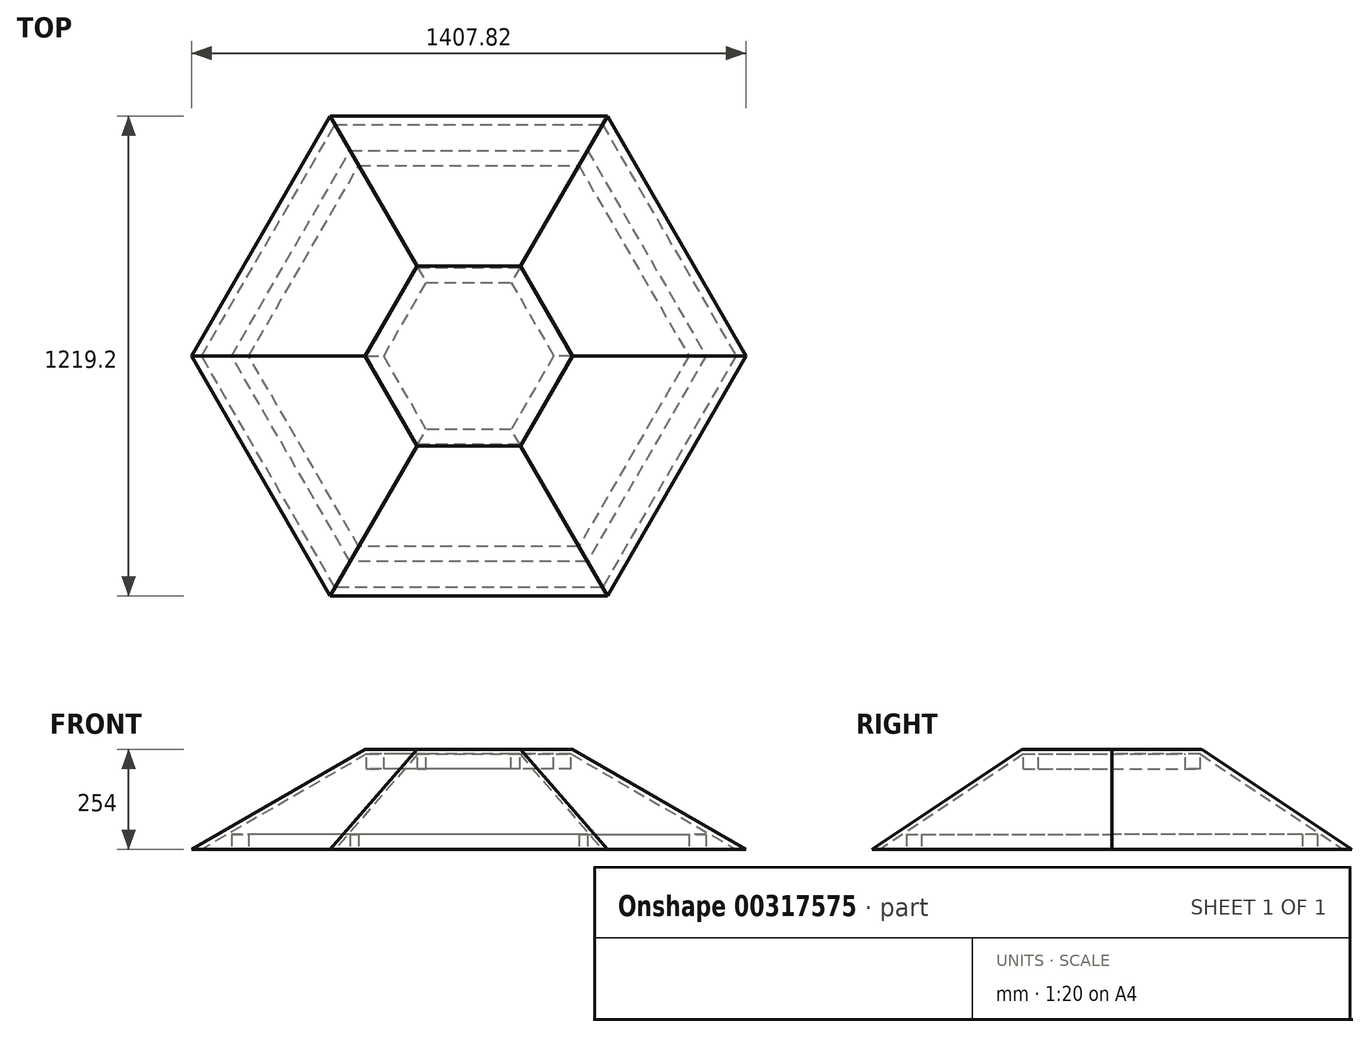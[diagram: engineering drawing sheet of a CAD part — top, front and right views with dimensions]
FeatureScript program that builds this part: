
annotation { "Feature Type Name" : "Feature", "Feature Type Description" : "" }
export const myFeature = defineFeature(function(context is Context, id is Id, definition is map)
    precondition{}
    {
        {
            var Q0;
            Q0=qCreatedBy(makeId("Top.planeOp"),FACE);
            var sketch = newSketch(context, id + "F0", { "sketchPlane" : qUnion([Q0])});
            skCircle(sketch, "E0.cCircle", {"center": v(0, 0) * mm, "radius": 609.6 * mm, "construction": true});
            skLineSegment(sketch, "E0.0", {"start": v(703.9, 0) * mm, "end": v(351.95, -609.6) * mm});
            skLineSegment(sketch, "E0.1", {"start": v(351.95, -609.6) * mm, "end": v(-351.95, -609.6) * mm});
            skLineSegment(sketch, "E0.2", {"start": v(-351.95, -609.6) * mm, "end": v(-703.9, 0) * mm});
            skLineSegment(sketch, "E0.3", {"start": v(-703.9, 0) * mm, "end": v(-351.95, 609.6) * mm});
            skLineSegment(sketch, "E0.4", {"start": v(-351.95, 609.6) * mm, "end": v(351.95, 609.6) * mm});
            skLineSegment(sketch, "E0.5", {"start": v(351.95, 609.6) * mm, "end": v(703.9, 0) * mm});
            skPoint(sketch, "E0.0.midPoint", {"position": v(527.93, -304.8) * mm});
            skSolve(sketch);
        }
        {
            var Q0;
            Q0=qCreatedBy(makeId("Front.planeOp"),FACE);
            var sketch = newSketch(context, id + "F1", { "sketchPlane" : qUnion([Q0])});
            skPoint(sketch, "E1.0", {"position": v(-703.9, 0) * mm});
            skPoint(sketch, "E2.0", {"position": v(703.9, 0) * mm});
            skLineSegment(sketch, "E3", {"start": v(703.9, 0) * mm, "end": v(263.96, 254) * mm});
            skLineSegment(sketch, "E4", {"start": v(263.96, 254) * mm, "end": v(-263.96, 254) * mm});
            skLineSegment(sketch, "E5", {"start": v(-263.96, 254) * mm, "end": v(-703.9, 0) * mm});
            skLineSegment(sketch, "E6", {"start": v(0, 0) * mm, "end": v(0, 391.16) * mm, "construction": true});
            skPoint(sketch, "E6.endSnap0", {"position": v(0, 254) * mm});
            skSolve(sketch);
        }
        {
            var Q0;
            Q0=makeQuery(id+"F0.imprint","IMPRINT",FACE,{"disambiguationData":[TD([[makeQuery(id+"F0.imprint","IMPRINT",EDGE,{"derivedFrom":sQuery(id+"F0.wireOp",EDGE,"E0.0")}),-1.0]])]});
            cPlane(context, id + "F2", {"entities" : qUnion([Q0]), "cplaneType" : CPlaneType.OFFSET, "offset" : 254 * mm, "width" : 152.4 * mm, "height" : 152.4 * mm});
        }
        {
            var Q0;
            Q0=qCreatedBy(id+"F2.planeOp",FACE);
            var sketch = newSketch(context, id + "F3", { "sketchPlane" : qUnion([Q0])});
            skCircle(sketch, "E7.cCircle", {"center": v(0, 0) * mm, "radius": 228.6 * mm, "construction": true});
            skLineSegment(sketch, "E7.0", {"start": v(263.96, 0) * mm, "end": v(131.98, -228.6) * mm});
            skLineSegment(sketch, "E7.1", {"start": v(131.98, -228.6) * mm, "end": v(-131.98, -228.6) * mm});
            skLineSegment(sketch, "E7.2", {"start": v(-131.98, -228.6) * mm, "end": v(-263.96, 0) * mm});
            skLineSegment(sketch, "E7.3", {"start": v(-263.96, 0) * mm, "end": v(-131.98, 228.6) * mm});
            skLineSegment(sketch, "E7.4", {"start": v(-131.98, 228.6) * mm, "end": v(131.98, 228.6) * mm});
            skLineSegment(sketch, "E7.5", {"start": v(131.98, 228.6) * mm, "end": v(263.96, 0) * mm});
            skPoint(sketch, "E7.0.midPoint", {"position": v(228.6, 0) * mm});
            skSolve(sketch);
        }
        {
            var Q0;
            Q0=makeQuery(id+"F3.imprint","IMPRINT",FACE,{"disambiguationData":[TD([[makeQuery(id+"F3.imprint","IMPRINT",EDGE,{"derivedFrom":sQuery(id+"F3.wireOp",EDGE,"E7.0")}),-1.0]])]});
            var Q1;
            Q1=makeQuery(id+"F0.imprint","IMPRINT",FACE,{"disambiguationData":[TD([[makeQuery(id+"F0.imprint","IMPRINT",EDGE,{"derivedFrom":sQuery(id+"F0.wireOp",EDGE,"E0.0")}),-1.0]])]});
            var Q2;
            Q2=sQuery(id+"F0.wireOp",VERTEX,"E0.2.start");
            var Q3;
            Q3=sQuery(id+"F3.wireOp",VERTEX,"E7.2.start");
            loft(context, id + "F4", {"sheetProfilesArray" : [{ "sheetProfileEntities" : qUnion([Q0]) }, { "sheetProfileEntities" : qUnion([Q1]) }], "connections" : [{ "connectionEntities" : qUnion([Q2, Q3]), "connectionEdgeQueries" : qUnion([]), "connectionEdgeParameters" : [] }]});
        }
        {
            var Q0;
            Q0=makeQuery(id+"F4.opLoft","CAP_FACE",FACE,{"disambiguationData":[OSD([makeQuery(id+"F0.imprint","IMPRINT",FACE,{"disambiguationData":[TD([[makeQuery(id+"F0.imprint","IMPRINT",EDGE,{"derivedFrom":sQuery(id+"F0.wireOp",EDGE,"E0.0")}),-1.0]])]})])],"isStart":true});
            shell(context, id + "F5", {"entities" : qUnion([Q0]), "thickness" : 11.9 * mm});
        }
        {
            var Q0;
            Q0=makeQuery(id+"F5.opShell","OFFSET_FACE",FACE,{"disambiguationData":[OSD([makeQuery(id+"F3.imprint","IMPRINT",FACE,{"disambiguationData":[TD([[makeQuery(id+"F3.imprint","IMPRINT",EDGE,{"derivedFrom":sQuery(id+"F3.wireOp",EDGE,"E7.0")}),-1.0]])]})])]});
            var sketch = newSketch(context, id + "F6", { "sketchPlane" : qUnion([Q0])});
            skLineSegment(sketch, "E8.0", {"start": v(-129.9, -225) * mm, "end": v(129.9, -225) * mm});
            skLineSegment(sketch, "E9.0", {"start": v(-107.9, -186.9) * mm, "end": v(107.9, -186.9) * mm});
            skLineSegment(sketch, "E10", {"start": v(-129.9, -225) * mm, "end": v(-107.9, -186.9) * mm});
            skLineSegment(sketch, "E11", {"start": v(129.9, -225) * mm, "end": v(107.9, -186.9) * mm});
            skSolve(sketch);
        }
        {
            var Q0;
            Q0=makeQuery(id+"F6.imprint","IMPRINT",FACE,{"disambiguationData":[TD([[makeQuery(id+"F6.imprint","IMPRINT",EDGE,{"derivedFrom":sQuery(id+"F6.wireOp",EDGE,"E8.0")}),1.0]])]});
            extrude(context, id + "F7", {"entities" : qUnion([Q0]), "depth" : 38.1 * mm});
        }
        {
            var Q0;
            Q0=makeQuery(id+"F0.imprint","IMPRINT",FACE,{"disambiguationData":[TD([[makeQuery(id+"F0.imprint","IMPRINT",EDGE,{"derivedFrom":sQuery(id+"F0.wireOp",EDGE,"E0.0")}),-1.0]])]});
            var sketch = newSketch(context, id + "F8", { "sketchPlane" : qUnion([Q0])});
            skLineSegment(sketch, "E12.0", {"start": v(-339.56, 588.14) * mm, "end": v(339.56, 588.14) * mm});
            skLineSegment(sketch, "E13.0", {"start": v(-301.48, 522.17) * mm, "end": v(301.48, 522.17) * mm});
            skLineSegment(sketch, "E14.0", {"start": v(-279.48, 484.07) * mm, "end": v(279.48, 484.07) * mm});
            skLineSegment(sketch, "E15", {"start": v(-301.48, 522.17) * mm, "end": v(-279.48, 484.07) * mm});
            skLineSegment(sketch, "E16", {"start": v(301.48, 522.17) * mm, "end": v(279.48, 484.07) * mm});
            skSolve(sketch);
        }
        {
            var Q0;
            Q0=makeQuery(id+"F8.imprint","IMPRINT",FACE,{"disambiguationData":[TD([[makeQuery(id+"F8.imprint","IMPRINT",EDGE,{"derivedFrom":sQuery(id+"F8.wireOp",EDGE,"E13.0")}),-1.0]])]});
            extrude(context, id + "F9", {"entities" : qUnion([Q0]), "operationType" : NewBodyOperationType.ADD, "depth" : 38.1 * mm});
        }
        {
            var Q0;
            Q0=makeQuery(id+"F7.opExtrude","SWEPT_BODY",BODY,{"disambiguationData":[OSD([sQuery(id+"F6.wireOp",EDGE,"E8.0"),sQuery(id+"F6.wireOp",EDGE,"E9.0"),sQuery(id+"F6.wireOp",EDGE,"E10"),sQuery(id+"F6.wireOp",EDGE,"E11")])]});
            var Q1;
            Q1=makeQuery(id+"F9.opExtrude","SWEPT_BODY",BODY,{"disambiguationData":[OSD([sQuery(id+"F8.wireOp",EDGE,"E13.0"),sQuery(id+"F8.wireOp",EDGE,"E14.0"),sQuery(id+"F8.wireOp",EDGE,"E15"),sQuery(id+"F8.wireOp",EDGE,"E16")])]});
            var Q2;
            Q2=sQuery(id+"F1.wireOp",EDGE,"E6");
            circularPattern(context, id + "F10", {"entities" : qUnion([Q0, Q1]), "axis" : qUnion([Q2]), "angle" : 360 * degree, "instanceCount" : 6, "equalSpace" : true});
        }
    });
